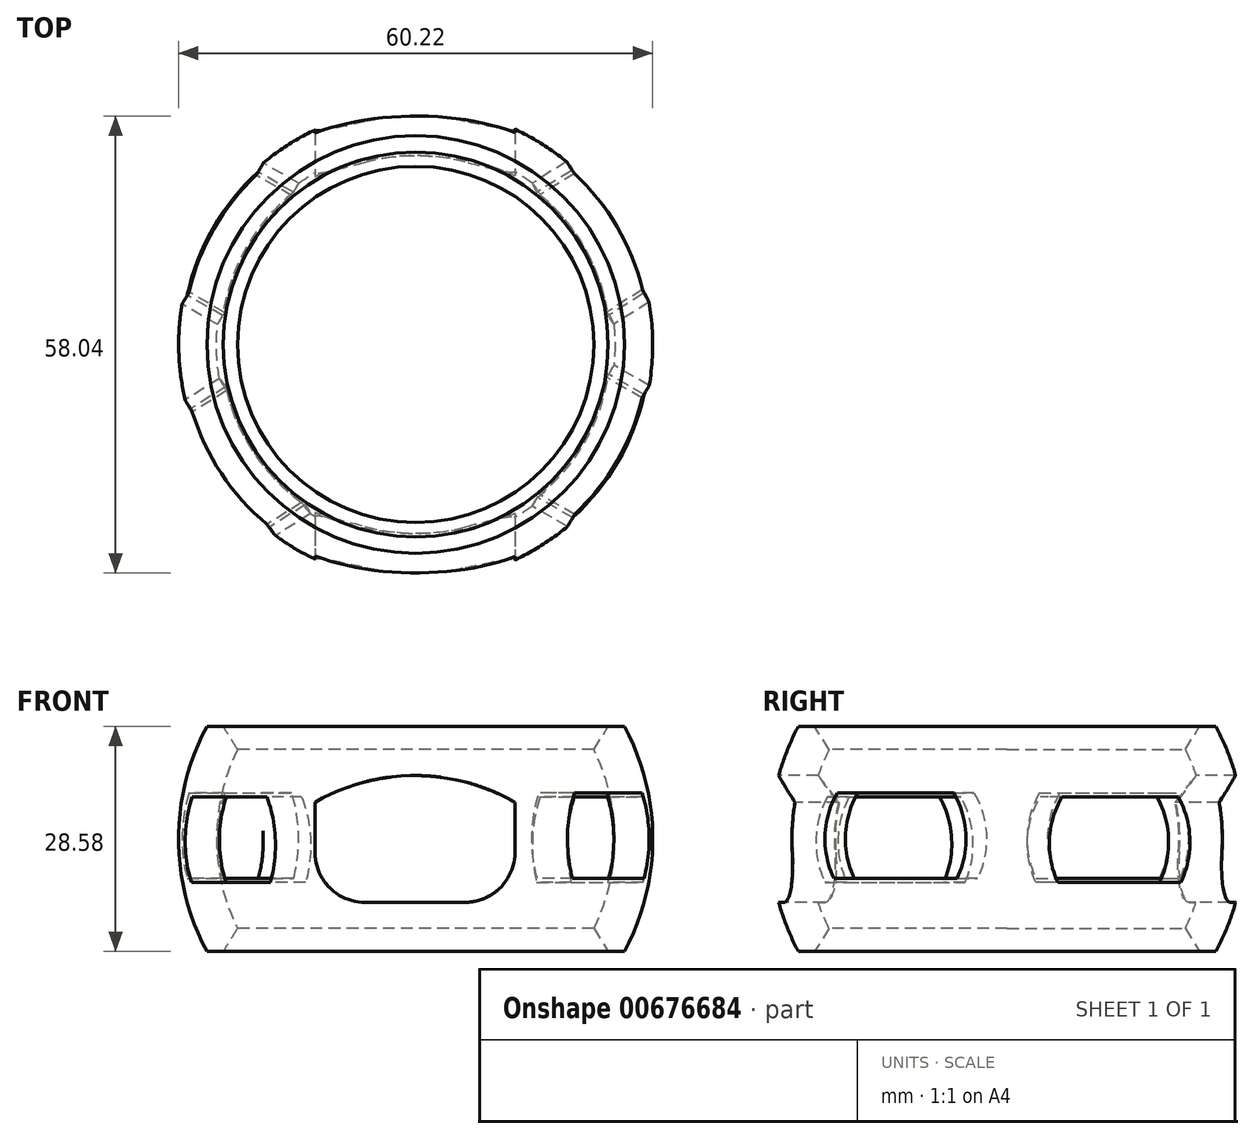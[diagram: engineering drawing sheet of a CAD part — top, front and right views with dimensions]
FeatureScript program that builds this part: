
annotation { "Feature Type Name" : "Feature", "Feature Type Description" : "" }
export const myFeature = defineFeature(function(context is Context, id is Id, definition is map)
    precondition{}
    {
        {
            var Q0;
            Q0=qCreatedBy(makeId("Front.planeOp"),FACE);
            var sketch = newSketch(context, id + "F0", { "sketchPlane" : qUnion([Q0])});
            skArc(sketch, "E0", {"start": v(26.61, -14.29) * mm, "mid": v(30.2, 0) * mm, "end": v(26.61, 14.29) * mm});
            skArc(sketch, "E1", {"start": v(21, -14.29) * mm, "mid": v(25.4, 0) * mm, "end": v(21, 14.29) * mm});
            skLineSegment(sketch, "E2", {"start": v(21, 14.29) * mm, "end": v(26.61, 14.29) * mm});
            skLineSegment(sketch, "E3", {"start": v(21, -14.29) * mm, "end": v(26.61, -14.29) * mm});
            skSolve(sketch);
        }
        {
            var Q0;
            Q0=qCreatedBy(makeId("Front.planeOp"),FACE);
            var sketch = newSketch(context, id + "F1", { "sketchPlane" : qUnion([Q0])});
            skLineSegment(sketch, "E4", {"start": v(0.1, 0.1) * mm, "end": v(0.1, 32.32) * mm});
            skSolve(sketch);
        }
        {
            var Q0;
            Q0=makeQuery(id+"F0.imprint","IMPRINT",FACE,{"disambiguationData":[TD([[makeQuery(id+"F0.imprint","IMPRINT",EDGE,{"derivedFrom":sQuery(id+"F0.wireOp",EDGE,"E0")}),1.0]])]});
            var Q1;
            Q1=sQuery(id+"F1.wireOp",EDGE,"E4");
            revolve(context, id + "F2", {"entities" : qUnion([Q0]), "axis" : qUnion([Q1]), "revolveType" : RevolveType.FULL});
        }
        {
            var Q0;
            Q0=makeQuery(id+"F2.opRevolve","SWEPT_EDGE",EDGE,{"disambiguationData":[OSD([sQuery(id+"F0.wireOp",EDGE,"E1"),sQuery(id+"F0.wireOp",EDGE,"E2")])]});
            var Q1;
            Q1=makeQuery(id+"F2.opRevolve","SWEPT_EDGE",EDGE,{"disambiguationData":[OSD([sQuery(id+"F0.wireOp",EDGE,"E1"),sQuery(id+"F0.wireOp",EDGE,"E3")])]});
            chamfer(context, id + "F3", {"entities" : qUnion([Q0, Q1]), "width" : 2.03 * mm, "tangentPropagation" : true});
        }
        {
            var Q0;
            Q0=qCreatedBy(makeId("Top.planeOp"),FACE);
            var sketch = newSketch(context, id + "F4", { "sketchPlane" : qUnion([Q0])});
            skCircle(sketch, "E5", {"center": v(0, 0) * mm, "radius": 23.02 * mm});
            skSolve(sketch);
        }
        {
            var Q0;
            Q0=qCreatedBy(makeId("Front.planeOp"),FACE);
            var sketch = newSketch(context, id + "F5", { "sketchPlane" : qUnion([Q0])});
            skLineSegment(sketch, "E6.bottom", {"start": v(-12.7, 4.65) * mm, "end": v(12.7, 4.65) * mm});
            skLineSegment(sketch, "E6.top", {"start": v(-6.35, -8.05) * mm, "end": v(6.35, -8.05) * mm});
            skLineSegment(sketch, "E6.left", {"start": v(-12.7, 4.65) * mm, "end": v(-12.7, -1.7) * mm});
            skLineSegment(sketch, "E6.right", {"start": v(12.7, 4.65) * mm, "end": v(12.7, -1.7) * mm});
            skArc(sketch, "E7", {"start": v(12.7, 4.65) * mm, "mid": v(0, 8.05) * mm, "end": v(-12.7, 4.65) * mm});
            skCircle(sketch, "E8", {"center": v(-6.35, -1.7) * mm, "radius": 6.35 * mm});
            skCircle(sketch, "E9", {"center": v(6.35, -1.7) * mm, "radius": 6.35 * mm});
            skLineSegment(sketch, "E10", {"start": v(0, 0) * mm, "end": v(0, -14.29) * mm});
            skPoint(sketch, "E10.endSnap0", {"position": v(0, -8.05) * mm});
            skPoint(sketch, "E11.orphan", {"position": v(12.7, -8.05) * mm});
            skPoint(sketch, "E12.orphan", {"position": v(-12.7, -8.05) * mm});
            skLineSegment(sketch, "E13", {"start": v(0, 8.05) * mm, "end": v(0, -8.05) * mm});
            skLineSegment(sketch, "E14", {"start": v(0, 0) * mm, "end": v(2.1, 0) * mm});
            skSolve(sketch);
        }
        {
            var Q0;
            {var subQ0=sQuery(id+"F5.wireOp",EDGE,"E9");var subQ1=sQuery(id+"F5.wireOp",EDGE,"E6.top");var subQ2=makeQuery(id+"F5.imprint","INTERSECT",VERTEX,{"derivedFrom":[subQ1,subQ0]});Q0=makeQuery(id+"F5.imprint","IMPRINT",FACE,{"disambiguationData":[TD([[makeQuery(id+"F5.imprint","IMPRINT",EDGE,{"disambiguationData":[TD([[subQ2,1.0]])],"derivedFrom":subQ1}),1.0]])]});}
            var Q1;
            {var subQ0=sQuery(id+"F5.wireOp",EDGE,"E8");var subQ1=sQuery(id+"F5.wireOp",EDGE,"E6.top");var subQ2=makeQuery(id+"F5.imprint","INTERSECT",VERTEX,{"derivedFrom":[subQ1,subQ0]});Q1=makeQuery(id+"F5.imprint","IMPRINT",FACE,{"disambiguationData":[TD([[makeQuery(id+"F5.imprint","IMPRINT",EDGE,{"disambiguationData":[TD([[subQ2,-1.0]])],"derivedFrom":subQ1}),1.0]])]});}
            var Q2;
            {var subQ0=sQuery(id+"F5.wireOp",EDGE,"E9");var subQ5=makeQuery(id+"F5.imprint","INTERSECT",VERTEX,{"derivedFrom":[sQuery(id+"F5.wireOp",EDGE,"E6.right"),subQ0]});Q2=makeQuery(id+"F5.imprint","IMPRINT",FACE,{"disambiguationData":[TD([[makeQuery(id+"F5.imprint","IMPRINT",EDGE,{"disambiguationData":[TD([[subQ5,-1.0]])],"derivedFrom":subQ0}),1.0]])]});}
            var Q3;
            {var subQ0=sQuery(id+"F5.wireOp",EDGE,"E8");var subQ3=makeQuery(id+"F5.imprint","INTERSECT",VERTEX,{"derivedFrom":[sQuery(id+"F5.wireOp",EDGE,"E6.left"),subQ0]});Q3=makeQuery(id+"F5.imprint","IMPRINT",FACE,{"disambiguationData":[TD([[makeQuery(id+"F5.imprint","IMPRINT",EDGE,{"disambiguationData":[TD([[subQ3,1.0]])],"derivedFrom":subQ0}),1.0]])]});}
            var Q4;
            {var subQ0=sQuery(id+"F5.wireOp",EDGE,"E6.right");Q4=makeQuery(id+"F5.imprint","IMPRINT",FACE,{"disambiguationData":[TD([[makeQuery(id+"F5.imprint","IMPRINT",EDGE,{"derivedFrom":subQ0}),-1.0]])]});}
            var Q5;
            {var subQ0=sQuery(id+"F5.wireOp",EDGE,"E6.left");Q5=makeQuery(id+"F5.imprint","IMPRINT",FACE,{"disambiguationData":[TD([[makeQuery(id+"F5.imprint","IMPRINT",EDGE,{"derivedFrom":subQ0}),1.0]])]});}
            var Q6;
            {var subQ0=sQuery(id+"F5.wireOp",EDGE,"E13");var subQ1=sQuery(id+"F5.wireOp",EDGE,"E6.bottom");var subQ2=makeQuery(id+"F5.imprint","INTERSECT",VERTEX,{"derivedFrom":[subQ1,subQ0]});Q6=makeQuery(id+"F5.imprint","IMPRINT",FACE,{"disambiguationData":[TD([[makeQuery(id+"F5.imprint","IMPRINT",EDGE,{"disambiguationData":[TD([[subQ2,-1.0]])],"derivedFrom":subQ1}),-1.0]])]});}
            var Q7;
            {var subQ0=sQuery(id+"F5.wireOp",EDGE,"E13");var subQ1=sQuery(id+"F5.wireOp",EDGE,"E6.bottom");var subQ2=makeQuery(id+"F5.imprint","INTERSECT",VERTEX,{"derivedFrom":[subQ1,subQ0]});Q7=makeQuery(id+"F5.imprint","IMPRINT",FACE,{"disambiguationData":[TD([[makeQuery(id+"F5.imprint","IMPRINT",EDGE,{"disambiguationData":[TD([[subQ2,-1.0]])],"derivedFrom":subQ1}),1.0]])]});}
            var Q8;
            {var subQ0=sQuery(id+"F5.wireOp",EDGE,"E8");var subQ1=sQuery(id+"F5.wireOp",EDGE,"E6.bottom");var subQ2=makeQuery(id+"F5.imprint","INTERSECT",VERTEX,{"derivedFrom":[subQ1,subQ0]});Q8=makeQuery(id+"F5.imprint","IMPRINT",FACE,{"disambiguationData":[TD([[makeQuery(id+"F5.imprint","IMPRINT",EDGE,{"disambiguationData":[TD([[subQ2,-1.0]])],"derivedFrom":subQ1}),-1.0]])]});}
            var Q9;
            {var subQ1=sQuery(id+"F5.wireOp",EDGE,"E6.bottom");var subQ3=makeQuery(id+"F5.imprint","INTERSECT",VERTEX,{"derivedFrom":[subQ1,sQuery(id+"F5.wireOp",EDGE,"E8")]});Q9=makeQuery(id+"F5.imprint","IMPRINT",FACE,{"disambiguationData":[TD([[makeQuery(id+"F5.imprint","IMPRINT",EDGE,{"disambiguationData":[TD([[subQ3,-1.0]])],"derivedFrom":subQ1}),1.0]])]});}
            var Q10;
            {var subQ0=sQuery(id+"F5.wireOp",EDGE,"E14");var subQ3=sQuery(id+"F5.wireOp",EDGE,"E13");var subQ5=makeQuery(id+"F5.imprint","INTERSECT",VERTEX,{"derivedFrom":[subQ3,subQ0]});Q10=makeQuery(id+"F5.imprint","IMPRINT",FACE,{"disambiguationData":[TD([[makeQuery(id+"F5.imprint","IMPRINT",EDGE,{"disambiguationData":[TD([[subQ5,-1.0]])],"derivedFrom":subQ0}),-1.0]])]});}
            extrude(context, id + "F6", {"entities" : qUnion([Q0, Q1, Q2, Q3, Q4, Q5, Q6, Q7, Q8, Q9, Q10]), "operationType" : NewBodyOperationType.REMOVE, "endBound" : BoundingType.SYMMETRIC, "oppositeDirection" : true, "depth" : 76.2 * mm, "offsetDistance" : 25.4 * mm});
        }
        {
            var Q0;
            Q0=qCreatedBy(makeId("Top.planeOp"),FACE);
            var sketch = newSketch(context, id + "F7", { "sketchPlane" : qUnion([Q0])});
            skLineSegment(sketch, "E15", {"start": v(0, 0) * mm, "end": v(33.1, 19.1) * mm});
            skLineSegment(sketch, "E16", {"start": v(0, 0) * mm, "end": v(-48.32, 27.9) * mm});
            skLineSegment(sketch, "E17", {"start": v(0, 0) * mm, "end": v(-43.24, -27.02) * mm});
            skLineSegment(sketch, "E18", {"start": v(0, 0) * mm, "end": v(52.32, -30.2) * mm});
            skLineSegment(sketch, "E19", {"start": v(0, 0) * mm, "end": v(55.6, 0) * mm});
            skLineSegment(sketch, "E20", {"start": v(0, 0) * mm, "end": v(-49.33, 0) * mm});
            skLineSegment(sketch, "E21", {"start": v(26.16, 15.1) * mm, "end": v(13.78, 36.55) * mm});
            skLineSegment(sketch, "E22", {"start": v(-26.15, 15.1) * mm, "end": v(-13.77, 36.55) * mm});
            skLineSegment(sketch, "E23", {"start": v(-25.62, -16) * mm, "end": v(-11.74, -38.22) * mm});
            skLineSegment(sketch, "E24", {"start": v(26.16, -15.1) * mm, "end": v(13.6, -36.87) * mm});
            skSolve(sketch);
        }
        {
            var Q0;
            Q0=sQuery(id+"F7.wireOp",EDGE,"E22");
            cPlane(context, id + "F8", {"entities" : qUnion([Q0]), "cplaneType" : CPlaneType.LINE_ANGLE, "offset" : 25.4 * mm, "angle" : 90 * degree, "width" : 152.4 * mm, "height" : 152.4 * mm});
        }
        {
            var Q0;
            Q0=sQuery(id+"F7.wireOp",EDGE,"E23");
            cPlane(context, id + "F9", {"entities" : qUnion([Q0]), "cplaneType" : CPlaneType.LINE_ANGLE, "offset" : 25.4 * mm, "angle" : 90 * degree, "width" : 152.4 * mm, "height" : 152.4 * mm});
        }
        {
            var Q0;
            Q0=qCreatedBy(id+"F8.planeOp",FACE);
            var sketch = newSketch(context, id + "F10", { "sketchPlane" : qUnion([Q0])});
            skArc(sketch, "E25", {"start": v(-8.56, 5.82) * mm, "mid": v(-10.34, 0.46) * mm, "end": v(-9.04, -5.04) * mm});
            skLineSegment(sketch, "E26", {"start": v(8.56, 5.82) * mm, "end": v(-8.56, 5.82) * mm});
            skLineSegment(sketch, "E27", {"start": v(0, -5.04) * mm, "end": v(9.04, -5.04) * mm});
            skLineSegment(sketch, "E28", {"start": v(9.04, -5.04) * mm, "end": v(-9.04, -5.04) * mm});
            skPoint(sketch, "E29.end.orphan", {"position": v(0, 5.82) * mm});
            skArc(sketch, "E30.trimOffspring", {"start": v(9.04, -5.04) * mm, "mid": v(10.34, 0.46) * mm, "end": v(8.56, 5.82) * mm});
            skSolve(sketch);
        }
        {
            var Q0;
            Q0 = qSketchRegion(id + "F10", true);
            extrude(context, id + "F11", {"entities" : qUnion([Q0]), "operationType" : NewBodyOperationType.REMOVE, "depth" : 76.2 * mm, "offsetDistance" : 25.4 * mm});
        }
        {
            var Q0;
            Q0=qCreatedBy(id+"F9.planeOp",FACE);
            var sketch = newSketch(context, id + "F12", { "sketchPlane" : qUnion([Q0])});
            skArc(sketch, "E31", {"start": v(-9.4, 5.31) * mm, "mid": v(-11.19, -0.05) * mm, "end": v(-9.89, -5.55) * mm});
            skLineSegment(sketch, "E32", {"start": v(7.7, 5.31) * mm, "end": v(-9.4, 5.31) * mm});
            skLineSegment(sketch, "E33", {"start": v(-0.85, -5.55) * mm, "end": v(8.19, -5.55) * mm});
            skLineSegment(sketch, "E34", {"start": v(8.19, -5.55) * mm, "end": v(-9.89, -5.55) * mm});
            skPoint(sketch, "E35.end.orphan", {"position": v(-0.85, 5.31) * mm});
            skArc(sketch, "E36.trimOffspring", {"start": v(8.19, -5.55) * mm, "mid": v(9.49, -0.05) * mm, "end": v(7.7, 5.31) * mm});
            skSolve(sketch);
        }
        {
            var Q0;
            Q0 = qSketchRegion(id + "F12", true);
            extrude(context, id + "F13", {"entities" : qUnion([Q0]), "operationType" : NewBodyOperationType.REMOVE, "depth" : 76.2 * mm, "offsetDistance" : 25.4 * mm});
        }
    });
